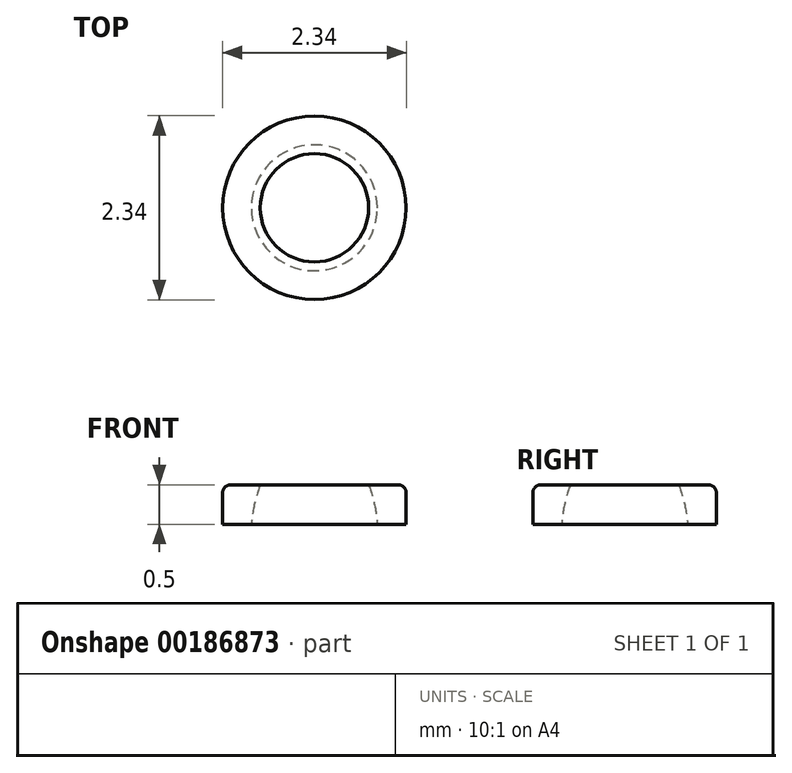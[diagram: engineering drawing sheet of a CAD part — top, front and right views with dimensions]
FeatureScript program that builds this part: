
annotation { "Feature Type Name" : "Feature", "Feature Type Description" : "" }
export const myFeature = defineFeature(function(context is Context, id is Id, definition is map)
    precondition{}
    {
        {
            var Q0;
            Q0=qCreatedBy(makeId("Top.planeOp"),FACE);
            var sketch = newSketch(context, id + "F0", { "sketchPlane" : qUnion([Q0])});
            skCircle(sketch, "E0", {"center": v(0, 0) * mm, "radius": 1.17 * mm});
            skSolve(sketch);
        }
        {
            var Q0;
            Q0=qCreatedBy(makeId("Front.planeOp"),FACE);
            var sketch = newSketch(context, id + "F1", { "sketchPlane" : qUnion([Q0])});
            skLineSegment(sketch, "E1", {"start": v(0, 1) * mm, "end": v(0.34, 1) * mm});
            skLineSegment(sketch, "E2", {"start": v(0, 0) * mm, "end": v(0.8, 0) * mm});
            skLineSegment(sketch, "E3", {"start": v(0, 1) * mm, "end": v(0, 0) * mm});
            skArc(sketch, "E4", {"start": v(0.44, 0.95) * mm, "mid": v(0.69, 0.5) * mm, "end": v(0.8, 0) * mm});
            skPoint(sketch, "E5.visualSharp", {"position": v(0.4, 1) * mm});
            skArc(sketch, "E5.filletArc", {"start": v(0.44, 0.95) * mm, "mid": v(0.4, 0.99) * mm, "end": v(0.34, 1) * mm});
            skLineSegment(sketch, "E6", {"start": v(0, 1.97) * mm, "end": v(0, -0.52) * mm, "construction": true});
            skSolve(sketch);
        }
        {
            var Q0;
            Q0 = qSketchRegion(id + "F0", true);
            extrude(context, id + "F2", {"entities" : qUnion([Q0]), "depth" : 0.5 * mm});
        }
        {
            var Q0;
            Q0=makeQuery(id+"F1.imprint","IMPRINT",FACE,{"disambiguationData":[TD([[makeQuery(id+"F1.imprint","IMPRINT",EDGE,{"derivedFrom":sQuery(id+"F1.wireOp",EDGE,"E1")}),-1.0]])]});
            var Q1;
            Q1=sQuery(id+"F1.wireOp",EDGE,"E6");
            revolve(context, id + "F3", {"operationType" : NewBodyOperationType.REMOVE, "entities" : qUnion([Q0]), "axis" : qUnion([Q1]), "revolveType" : RevolveType.FULL});
        }
        {
            var Q0;
            Q0=makeQuery(id+"F2.opExtrude","CAP_EDGE",EDGE,{"disambiguationData":[OSD([sQuery(id+"F0.wireOp",EDGE,"E0")])],"isStart":false});
            fillet(context, id + "F4", {"entities" : qUnion([Q0]), "radius" : 0.1 * mm, "tangentPropagation" : true, "allowEdgeOverflow" : false});
        }
    });
